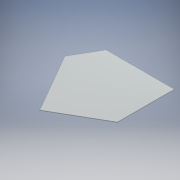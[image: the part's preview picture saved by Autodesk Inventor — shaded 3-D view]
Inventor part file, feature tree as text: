
AUTODESK INVENTOR PART (.ipt)
format: ipt  version: 2016 SP1 (Build 200210100, 210)  size: 166,400 bytes
history: native  units: mm
features: reference x3, extrude x1, sketch x1
ambient origin geometry x8: Origin, YZ Plane, XZ Plane, XY Plane, X Axis, Y Axis, Z Axis, Center Point
bodies: Solid1 (feature_tree)
feature tree (5):
  extrude  "Extrusion1"  [1 undecoded]
  sketch  "Sketch1"  dims[d0=1.5mm d1=0.0mm]
  reference  "Reference1"
  reference  "Reference2"
  reference  "Reference3"
note: 1 required parameter value undecoded (feature->parameter linkage not recoverable at this tier; creation-order binding heuristic only, values carry confidence <= 0.55)
